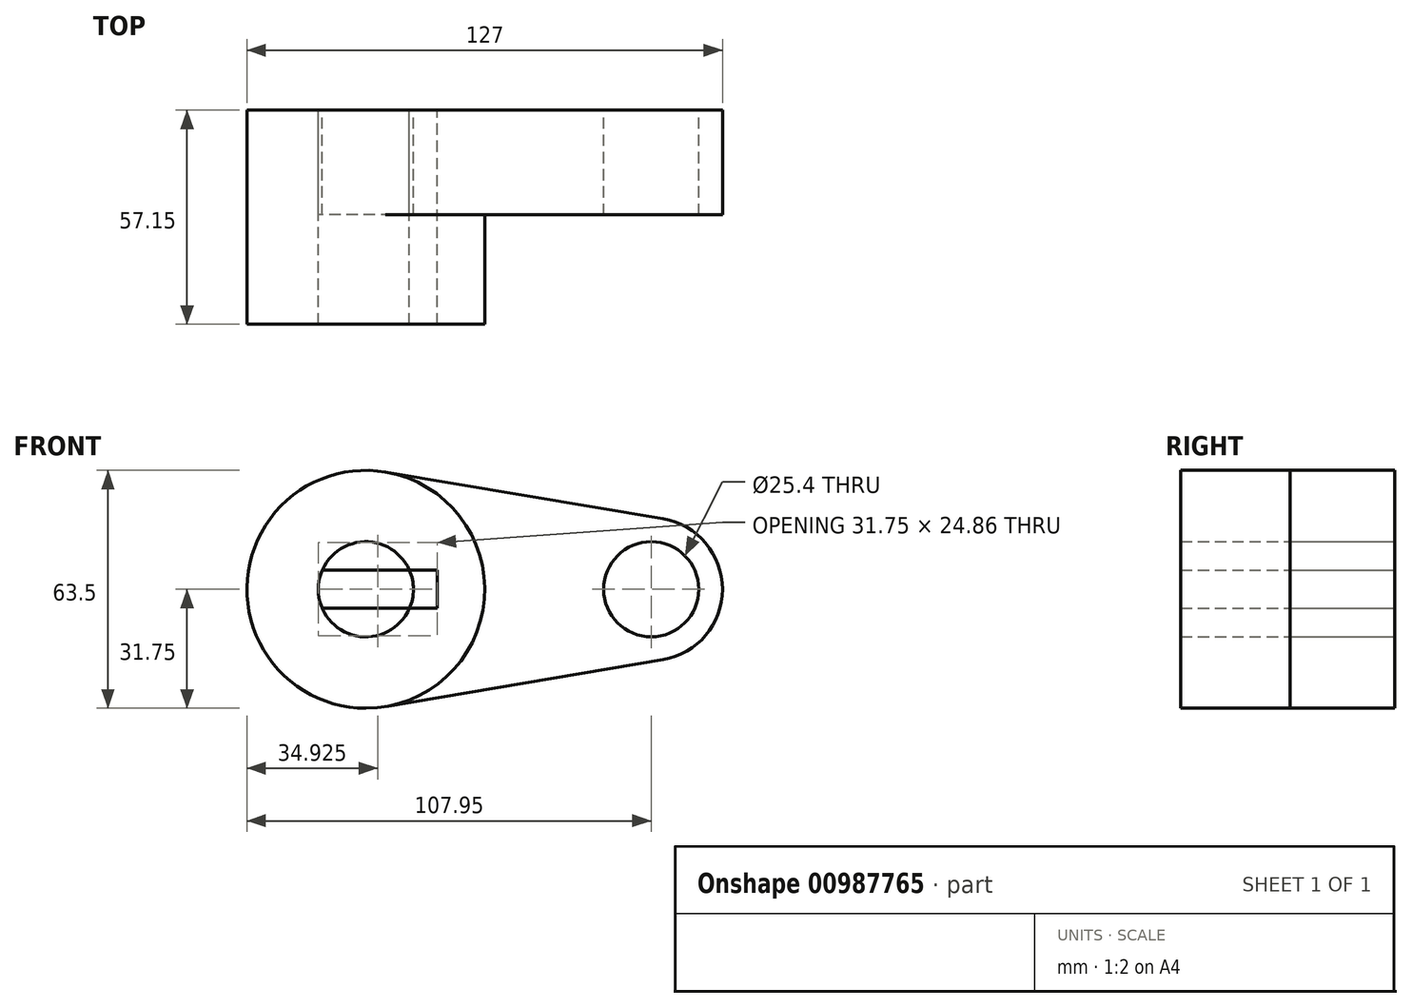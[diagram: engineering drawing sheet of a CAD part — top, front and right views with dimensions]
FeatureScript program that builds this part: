
annotation { "Feature Type Name" : "Feature", "Feature Type Description" : "" }
export const myFeature = defineFeature(function(context is Context, id is Id, definition is map)
    precondition{}
    {
        {
            var Q0;
            Q0=qCreatedBy(makeId("Front.planeOp"),FACE);
            var sketch = newSketch(context, id + "F0", { "sketchPlane" : qUnion([Q0])});
            skCircle(sketch, "E0", {"center": v(0, 0) * mm, "radius": 31.75 * mm});
            skCircle(sketch, "E1", {"center": v(76.2, 0) * mm, "radius": 19.05 * mm});
            skLineSegment(sketch, "E2", {"start": v(5.3, 31.3) * mm, "end": v(79.38, 18.78) * mm});
            skLineSegment(sketch, "E3", {"start": v(5.3, -31.3) * mm, "end": v(79.38, -18.78) * mm});
            skCircle(sketch, "E4", {"center": v(0, 0) * mm, "radius": 12.7 * mm});
            skCircle(sketch, "E5", {"center": v(76.2, 0) * mm, "radius": 12.7 * mm});
            skLineSegment(sketch, "E6.bottom", {"start": v(19.05, -5.08) * mm, "end": v(-19.05, -5.08) * mm});
            skLineSegment(sketch, "E6.top", {"start": v(19.05, 5.08) * mm, "end": v(-19.05, 5.08) * mm});
            skLineSegment(sketch, "E6.left", {"start": v(19.05, -5.08) * mm, "end": v(19.05, 5.08) * mm});
            skLineSegment(sketch, "E6.right", {"start": v(-19.05, -5.08) * mm, "end": v(-19.05, 5.08) * mm});
            skSolve(sketch);
        }
        {
            var Q0;
            {var subQ7=sQuery(id+"F0.wireOp",EDGE,"E6.left");Q0=makeQuery(id+"F0.imprint","IMPRINT",FACE,{"disambiguationData":[TD([[makeQuery(id+"F0.imprint","IMPRINT",EDGE,{"derivedFrom":subQ7}),-1.0]])]});}
            var Q1;
            {var subQ0=sQuery(id+"F0.wireOp",EDGE,"E6.bottom");var subQ1=sQuery(id+"F0.wireOp",EDGE,"E4");var subQ2=makeQuery(id+"F0.imprint","INTERSECT",VERTEX,{"disambiguationData":[OD(0.0)],"derivedFrom":[subQ1,subQ0]});Q1=makeQuery(id+"F0.imprint","IMPRINT",FACE,{"disambiguationData":[TD([[makeQuery(id+"F0.imprint","IMPRINT",EDGE,{"disambiguationData":[TD([[subQ2,-1.0]])],"derivedFrom":subQ1}),1.0]])]});}
            var Q2;
            {var subQ0=sQuery(id+"F0.wireOp",EDGE,"E2");Q2=makeQuery(id+"F0.imprint","IMPRINT",FACE,{"disambiguationData":[TD([[makeQuery(id+"F0.imprint","IMPRINT",EDGE,{"derivedFrom":subQ0}),-1.0]])]});}
            var Q3;
            Q3=makeQuery(id+"F0.imprint","IMPRINT",FACE,{"disambiguationData":[TD([[makeQuery(id+"F0.imprint","IMPRINT",EDGE,{"derivedFrom":sQuery(id+"F0.wireOp",EDGE,"E5")}),-1.0]])]});
            extrude(context, id + "F1", {"entities" : qUnion([Q0, Q1, Q2, Q3]), "depth" : 27.94 * mm, "offsetDistance" : 25.4 * mm});
        }
        {
            var Q0;
            {var subQ7=sQuery(id+"F0.wireOp",EDGE,"E6.left");Q0=makeQuery(id+"F0.imprint","IMPRINT",FACE,{"disambiguationData":[TD([[makeQuery(id+"F0.imprint","IMPRINT",EDGE,{"derivedFrom":subQ7}),-1.0]])]});}
            var Q1;
            {var subQ5=sQuery(id+"F0.wireOp",EDGE,"E6.right");Q1=makeQuery(id+"F0.imprint","IMPRINT",FACE,{"disambiguationData":[TD([[makeQuery(id+"F0.imprint","IMPRINT",EDGE,{"derivedFrom":subQ5}),-1.0]])]});}
            extrude(context, id + "F2", {"entities" : qUnion([Q0, Q1]), "operationType" : NewBodyOperationType.ADD, "depth" : 57.15 * mm, "offsetDistance" : 25.4 * mm});
        }
    });
